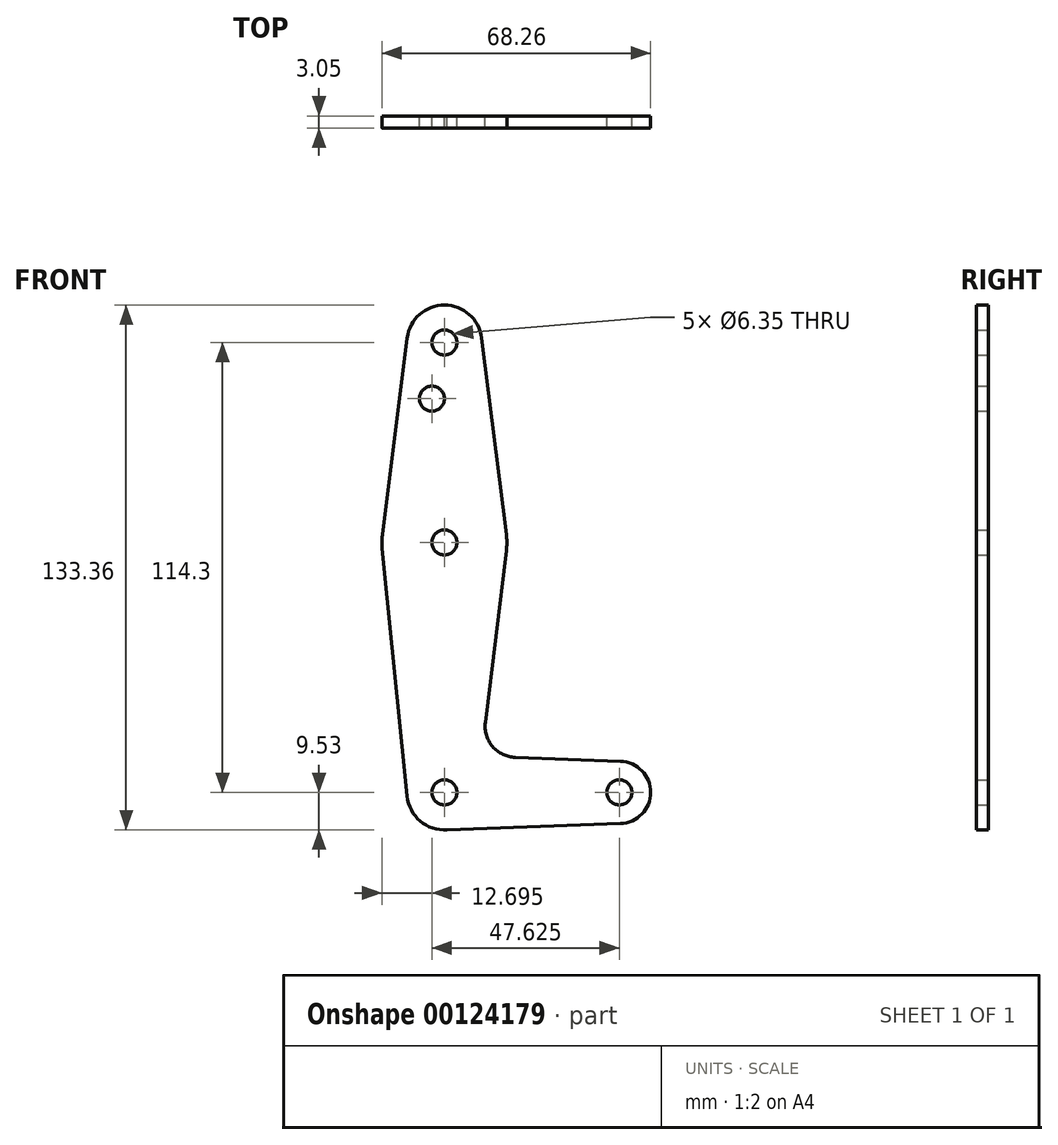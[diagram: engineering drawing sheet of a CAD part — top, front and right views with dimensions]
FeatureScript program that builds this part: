
annotation { "Feature Type Name" : "Feature", "Feature Type Description" : "" }
export const myFeature = defineFeature(function(context is Context, id is Id, definition is map)
    precondition{}
    {
        {
            var Q0;
            Q0=qCreatedBy(makeId("Front.planeOp"),FACE);
            var sketch = newSketch(context, id + "F0", { "sketchPlane" : qUnion([Q0])});
            skLineSegment(sketch, "E0", {"start": v(0, 0) * mm, "end": v(0, 114.3) * mm, "construction": true});
            skLineSegment(sketch, "E1", {"start": v(0, 0) * mm, "end": v(44.45, 0) * mm, "construction": true});
            skCircle(sketch, "E2", {"center": v(0, 114.3) * mm, "radius": 9.53 * mm});
            skCircle(sketch, "E3", {"center": v(0, 0) * mm, "radius": 9.53 * mm});
            skCircle(sketch, "E4", {"center": v(0, 63.5) * mm, "radius": 15.88 * mm});
            skCircle(sketch, "E5", {"center": v(44.45, 0) * mm, "radius": 7.94 * mm});
            skLineSegment(sketch, "E6", {"start": v(9.45, 115.5) * mm, "end": v(15.75, 65.48) * mm});
            skLineSegment(sketch, "E7", {"start": v(-9.45, 115.5) * mm, "end": v(-15.75, 65.48) * mm});
            skCircle(sketch, "E8", {"center": v(0, 114.3) * mm, "radius": 3.18 * mm});
            skCircle(sketch, "E9", {"center": v(0, 63.5) * mm, "radius": 3.18 * mm});
            skCircle(sketch, "E10", {"center": v(-3.18, 100.03) * mm, "radius": 3.18 * mm});
            skCircle(sketch, "E11", {"center": v(0, 0) * mm, "radius": 3.18 * mm});
            skCircle(sketch, "E12", {"center": v(44.45, 0) * mm, "radius": 3.18 * mm});
            skLineSegment(sketch, "E13.trimOffspring", {"start": v(9.57, 0) * mm, "end": v(9.48, -0.95) * mm});
            skLineSegment(sketch, "E14", {"start": v(-15.8, 61.91) * mm, "end": v(-9.48, -0.95) * mm});
            skLineSegment(sketch, "E15", {"start": v(15.76, 61.63) * mm, "end": v(10.4, 17.8) * mm});
            skLineSegment(sketch, "E16", {"start": v(0, -9.53) * mm, "end": v(44.73, -7.93) * mm});
            skLineSegment(sketch, "E17", {"start": v(18.02, 8.88) * mm, "end": v(44.73, 7.93) * mm});
            skArc(sketch, "E18.filletArc", {"start": v(10.4, 17.8) * mm, "mid": v(12.25, 11.67) * mm, "end": v(18.02, 8.88) * mm});
            skSolve(sketch);
        }
        {
            var Q0;
            Q0 = qSketchRegion(id + "F0", true);
            extrude(context, id + "F1", {"entities" : qUnion([Q0]), "depth" : 3.05 * mm});
        }
    });
